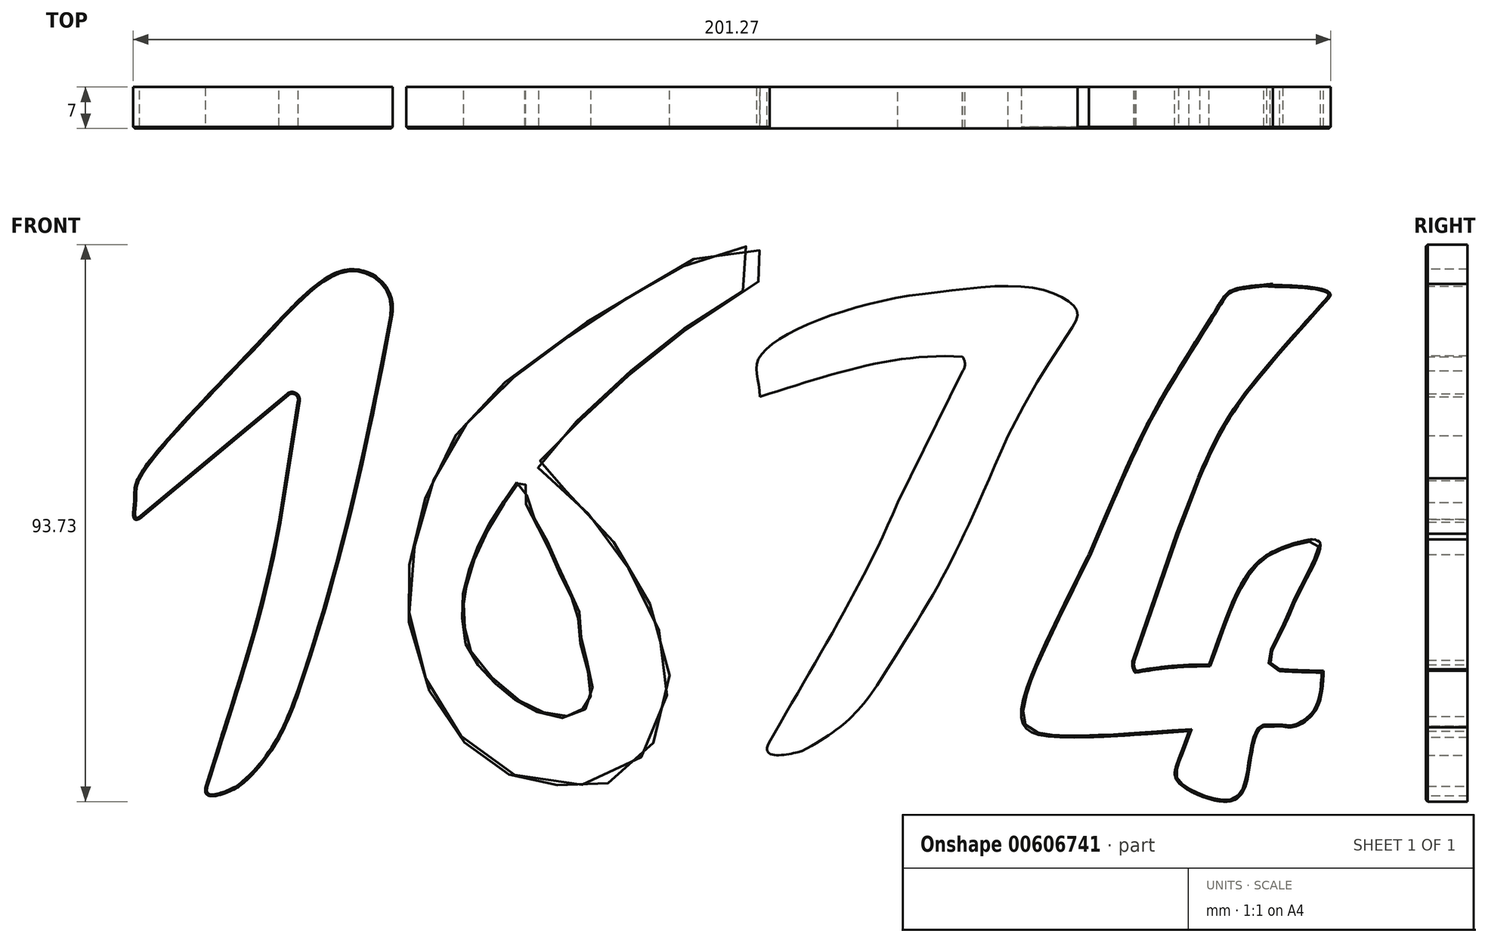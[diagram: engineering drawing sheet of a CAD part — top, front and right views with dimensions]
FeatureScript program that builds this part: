
annotation { "Feature Type Name" : "Feature", "Feature Type Description" : "" }
export const myFeature = defineFeature(function(context is Context, id is Id, definition is map)
    precondition{}
    {
        {
            var Q0;
            Q0=qCreatedBy(makeId("Front.planeOp"),FACE);
            var sketch = newSketch(context, id + "F0", { "sketchPlane" : qUnion([Q0])});
            skLineSegment(sketch, "E0", {"start": v(-92.68, 7.2) * mm, "end": v(-67.67, 28.04) * mm});
            skLineSegment(sketch, "E1", {"start": v(-66.04, 27.11) * mm, "end": v(-69.27, 6.68) * mm});
            skPoint(sketch, "E2.visualSharp", {"position": v(-65.63, 29.74) * mm});
            skArc(sketch, "E2.filletArc", {"start": v(-66.04, 27.11) * mm, "mid": v(-66.53, 28.14) * mm, "end": v(-67.67, 28.04) * mm});
            skFitSpline(sketch, "E3", {"points": [v(-69.27, 6.68) * mm, v(-81.5, -37.64) * mm], "startDerivative": vector(-8.47, -48.32) * mm, "endDerivative": vector(-12.86, -41.9) * mm});
            skFitSpline(sketch, "E4", {"points": [v(-81.5, -37.64) * mm, v(-75.88, -37.8) * mm], "startDerivative": vector(-3.5, -11.42) * mm, "endDerivative": vector(1.2, 0.98) * mm});
            skFitSpline(sketch, "E5", {"points": [v(-65.67, -21.29) * mm, v(-75.88, -37.8) * mm], "startDerivative": vector(-6.02, -17.7) * mm, "endDerivative": vector(-17.03, -13.98) * mm});
            skFitSpline(sketch, "E6", {"points": [v(-65.67, -21.29) * mm, v(-50.24, 41.3) * mm], "startDerivative": vector(20.8, 61.13) * mm, "endDerivative": vector(11.64, 63.63) * mm});
            skFitSpline(sketch, "E7", {"points": [v(-50.24, 41.3) * mm, v(-51.61, 46.83) * mm, v(-58.52, 49.02) * mm, v(-74.86, 34.62) * mm], "startDerivative": vector(4.33, 23.7) * mm, "endDerivative": vector(-40.7, -41.95) * mm});
            skFitSpline(sketch, "E8", {"points": [v(-74.86, 34.62) * mm, v(-93.57, 10.32) * mm, v(-93.56, 7.2) * mm, v(-92.68, 7.2) * mm], "startDerivative": vector(-91.04, -93.86) * mm, "endDerivative": vector(9, 3.05) * mm});
            skFitSpline(sketch, "E9", {"points": [v(-74.86, 34.62) * mm, v(-93.57, 10.32) * mm, v(-93.56, 7.2) * mm, v(-92.68, 7.2) * mm], "startDerivative": vector(-91.04, -93.86) * mm, "endDerivative": vector(9, 3.05) * mm});
            skLineSegment(sketch, "E10", {"start": v(-93.64, 7.35) * mm, "end": v(-93.32, 12.7) * mm});
            skLineSegment(sketch, "E11", {"start": v(-93.32, 12.7) * mm, "end": v(-93, 13.93) * mm});
            skSolve(sketch);
        }
        {
            var Q0;
            Q0=qCreatedBy(makeId("Front.planeOp"),FACE);
            var sketch = newSketch(context, id + "F1", { "sketchPlane" : qUnion([Q0])});
            skFitSpline(sketch, "E12", {"points": [v(-0.98, 38.94) * mm, v(13, 48.92) * mm, v(12.6, 51.28) * mm, v(8.34, 53.38) * mm, v(-20.6, 38.22) * mm, v(-36.6, 24.97) * mm, v(-43.36, 14.2) * mm, v(-47.04, 1.02) * mm, v(-47.76, -6.92) * mm, v(-44.74, -19.9) * mm, v(-39.1, -29.23) * mm, v(-32.6, -34.87) * mm, v(-25.78, -37.1) * mm, v(-19.74, -37.76) * mm, v(-12.33, -36.64) * mm, v(-5.3, -28.44) * mm, v(-4, -15.32) * mm, v(-9.9, -1.54) * mm, v(-17.38, 8.63) * mm, v(-25.06, 15.45) * mm, v(-25.47, 16.76) * mm, v(-20.09, 22.41) * mm, v(-11.63, 30.3) * mm, v(-0.98, 38.94) * mm]});
            skFitSpline(sketch, "E13", {"points": [v(-29.07, 13.15) * mm, v(-31.94, 8.9) * mm, v(-35.91, 1.66) * mm, v(-37.8, -4.45) * mm, v(-38.18, -6.71) * mm, v(-38.01, -11.23) * mm, v(-36.58, -15.81) * mm, v(-29.18, -23.1) * mm, v(-24.22, -25.52) * mm, v(-19.97, -25.86) * mm, v(-18.1, -24.7) * mm, v(-17.05, -23.43) * mm, v(-17.05, -19.46) * mm, v(-18.7, -13.11) * mm, v(-19.09, -8.42) * mm, v(-20.85, -4.5) * mm, v(-22.95, -0.03) * mm, v(-25.27, 5.04) * mm, v(-27.8, 10) * mm, v(-27.8, 13.04) * mm, v(-28.3, 13.64) * mm, v(-29.07, 13.15) * mm]});
            skSolve(sketch);
        }
        {
            var Q0;
            Q0=qCreatedBy(makeId("Front.planeOp"),FACE);
            var sketch = newSketch(context, id + "F2", { "sketchPlane" : qUnion([Q0])});
            skLineSegment(sketch, "E14", {"start": v(45.72, 32.14) * mm, "end": v(34.79, 9.97) * mm});
            skPoint(sketch, "E15.visualSharp", {"position": v(53.05, 42.63) * mm});
            skArc(sketch, "E15.filletArc", {"start": v(45.72, 32.14) * mm, "mid": v(46.07, 33.32) * mm, "end": v(45.66, 34.48) * mm});
            skFitSpline(sketch, "E16", {"points": [v(34.79, 9.97) * mm, v(13.12, -30.48) * mm], "startDerivative": vector(-19.16, -45.24) * mm, "endDerivative": vector(-21.62, -38.5) * mm});
            skFitSpline(sketch, "E17", {"points": [v(13.12, -30.48) * mm, v(18.63, -31.83) * mm], "startDerivative": vector(-5.9, -10.52) * mm, "endDerivative": vector(1.06, 0.55) * mm});
            skFitSpline(sketch, "E18", {"points": [v(31.7, -20.14) * mm, v(18.63, -31.83) * mm], "startDerivative": vector(-10.16, -16) * mm, "endDerivative": vector(-19.7, -10.23) * mm});
            skFitSpline(sketch, "E19", {"points": [v(31.7, -20.14) * mm, v(53.3, 21.22) * mm], "startDerivative": vector(34.21, 53.88) * mm, "endDerivative": vector(26.95, 62.38) * mm});
            skFitSpline(sketch, "E20", {"points": [v(53.3, 21.22) * mm, v(64.68, 42.59) * mm, v(58.21, 45.98) * mm, v(38.9, 45.06) * mm], "startDerivative": vector(64.2, 125.67) * mm, "endDerivative": vector(-57.63, -6.86) * mm});
            skFitSpline(sketch, "E21", {"points": [v(45.66, 34.48) * mm, v(11.57, 27.76) * mm], "startDerivative": vector(-33.68, 2.47) * mm, "endDerivative": vector(-35.46, -11.25) * mm});
            skFitSpline(sketch, "E22", {"points": [v(11.57, 27.76) * mm, v(11.57, 34.48) * mm, v(38.9, 45.06) * mm], "startDerivative": vector(0.24, 25.58) * mm, "endDerivative": vector(50, 5.96) * mm});
            skFitSpline(sketch, "E23", {"points": [v(45.66, 34.48) * mm, v(11.57, 27.76) * mm], "startDerivative": vector(-33.68, 2.47) * mm, "endDerivative": vector(-35.46, -11.25) * mm});
            skSolve(sketch);
        }
        {
            var Q0;
            Q0=qCreatedBy(makeId("Front.planeOp"),FACE);
            var sketch = newSketch(context, id + "F3", { "sketchPlane" : qUnion([Q0])});
            skLineSegment(sketch, "E24", {"start": v(74.6, -16.55) * mm, "end": v(81.93, 4.72) * mm});
            skPoint(sketch, "E25.visualSharp", {"position": v(67.27, -27.04) * mm});
            skArc(sketch, "E25.filletArc", {"start": v(74.6, -16.55) * mm, "mid": v(74.5, -17.48) * mm, "end": v(74.83, -18.36) * mm});
            skFitSpline(sketch, "E26", {"points": [v(83.32, 8.87) * mm, v(107.26, 44.32) * mm], "startDerivative": vector(19.16, 45.24) * mm, "endDerivative": vector(52.3, 57.7) * mm});
            skFitSpline(sketch, "E27", {"points": [v(107.26, 44.32) * mm, v(97.83, 46.76) * mm], "startDerivative": vector(8.1, 8.94) * mm, "endDerivative": vector(16.4, 1.55) * mm});
            skFitSpline(sketch, "E28", {"points": [v(87.26, 40.86) * mm, v(97.83, 46.76) * mm], "startDerivative": vector(10.16, 16) * mm, "endDerivative": vector(25.73, 2.44) * mm});
            skFitSpline(sketch, "E29", {"points": [v(87.26, 40.86) * mm, v(66.87, 1.25) * mm], "startDerivative": vector(-34.21, -53.88) * mm, "endDerivative": vector(-26.95, -62.38) * mm});
            skFitSpline(sketch, "E30", {"points": [v(66.87, 1.25) * mm, v(55.78, -27.18) * mm, v(62.85, -29.56) * mm, v(99.48, -27.7) * mm], "startDerivative": vector(-62.3, -126.61) * mm, "endDerivative": vector(58.88, -0.73) * mm});
            skFitSpline(sketch, "E31", {"points": [v(74.83, -18.36) * mm, v(106.36, -18.33) * mm], "startDerivative": vector(40.38, 7.12) * mm, "endDerivative": vector(38.72, 0) * mm});
            skFitSpline(sketch, "E32", {"points": [v(85.51, 14.03) * mm, v(81.93, 4.72) * mm], "startDerivative": vector(-3.58, -9.32) * mm, "endDerivative": vector(-3.58, -9.32) * mm});
            skFitSpline(sketch, "E33", {"points": [v(66.87, 1.25) * mm, v(55.78, -27.18) * mm, v(62.85, -29.56) * mm, v(99.48, -27.7) * mm], "startDerivative": vector(-62.3, -126.61) * mm, "endDerivative": vector(58.88, -0.73) * mm});
            skFitSpline(sketch, "E34", {"points": [v(87.1, -17.3) * mm, v(95.33, 0) * mm, v(102.56, 3.42) * mm, v(105.76, 3.24) * mm, v(102.25, -5.3) * mm, v(99.17, -12.02) * mm, v(98.95, -18.08) * mm], "startDerivative": vector(34.67, 99.65) * mm, "endDerivative": vector(63.85, -8.51) * mm});
            skFitSpline(sketch, "E35", {"points": [v(96.37, -27.75) * mm, v(94.1, -33.34) * mm, v(91.2, -40.14) * mm, v(82.22, -37.45) * mm, v(83.74, -28.5) * mm], "startDerivative": vector(-17.93, 0) * mm, "endDerivative": vector(24.99, 68.37) * mm});
            skFitSpline(sketch, "E36", {"points": [v(99.48, -27.7) * mm, v(101.43, -27.75) * mm, v(105.02, -25.02) * mm, v(106.36, -18.33) * mm], "startDerivative": vector(7.82, -1.52) * mm, "endDerivative": vector(0.86, 17.28) * mm});
            skSolve(sketch);
        }
        {
            var Q0;
            Q0 = qSketchRegion(id + "F0", true);
            var Q1;
            Q1 = qSketchRegion(id + "F1", true);
            var Q2;
            Q2 = qSketchRegion(id + "F2", true);
            var Q3;
            Q3 = qSketchRegion(id + "F3", true);
            extrude(context, id + "F4", {"entities" : qUnion([Q0, Q1, Q2, Q3]), "depth" : 7 * mm, "offsetDistance" : 25 * mm});
        }
        {
            var Q0;
            Q0=makeQuery(id+"F4.opExtrude","CAP_EDGE",EDGE,{"disambiguationData":[OSD([sQuery(id+"F0.wireOp",EDGE,"E8")])],"isStart":false});
            var Q1;
            Q1=makeQuery(id+"F4.opExtrude","CAP_EDGE",EDGE,{"disambiguationData":[OSD([sQuery(id+"F0.wireOp",EDGE,"E0")])],"isStart":false});
            var Q2;
            Q2=makeQuery(id+"F4.opExtrude","SWEPT_EDGE",EDGE,{"disambiguationData":[OSD([sQuery(id+"F0.wireOp",EDGE,"E10"),sQuery(id+"F0.wireOp",EDGE,"E11")])]});
            var Q3;
            Q3=makeQuery(id+"F4.opExtrude","SWEPT_EDGE",EDGE,{"disambiguationData":[OSD([sQuery(id+"F0.wireOp",EDGE,"E8"),sQuery(id+"F0.wireOp",EDGE,"E11")])]});
            var Q4;
            Q4=makeQuery(id+"F4.opExtrude","CAP_EDGE",EDGE,{"disambiguationData":[OSD([sQuery(id+"F1.wireOp",EDGE,"E12")])],"isStart":false});
            var Q5;
            Q5=makeQuery(id+"F4.opExtrude","CAP_EDGE",EDGE,{"disambiguationData":[OSD([sQuery(id+"F1.wireOp",EDGE,"E13")])],"isStart":false});
            var Q6;
            Q6=makeQuery(id+"F4.opExtrude","CAP_FACE",FACE,{"disambiguationData":[OSD([sQuery(id+"F2.wireOp",EDGE,"E14"),sQuery(id+"F2.wireOp",EDGE,"E15.filletArc"),sQuery(id+"F2.wireOp",EDGE,"E16"),sQuery(id+"F2.wireOp",EDGE,"E17"),sQuery(id+"F2.wireOp",EDGE,"E18"),sQuery(id+"F2.wireOp",EDGE,"E19"),sQuery(id+"F2.wireOp",EDGE,"E20"),sQuery(id+"F2.wireOp",EDGE,"E21"),sQuery(id+"F2.wireOp",EDGE,"E22"),sQuery(id+"F2.wireOp",EDGE,"E23")])],"isStart":false});
            var Q7;
            Q7=makeQuery(id+"F4.opExtrude","CAP_FACE",FACE,{"disambiguationData":[OSD([sQuery(id+"F3.wireOp",EDGE,"E24"),sQuery(id+"F3.wireOp",EDGE,"E25.filletArc"),sQuery(id+"F3.wireOp",EDGE,"E26"),sQuery(id+"F3.wireOp",EDGE,"E27"),sQuery(id+"F3.wireOp",EDGE,"E28"),sQuery(id+"F3.wireOp",EDGE,"E29"),sQuery(id+"F3.wireOp",EDGE,"E30"),sQuery(id+"F3.wireOp",EDGE,"E31"),sQuery(id+"F3.wireOp",EDGE,"E32"),sQuery(id+"F3.wireOp",EDGE,"E31"),sQuery(id+"F3.wireOp",EDGE,"E33"),sQuery(id+"F3.wireOp",EDGE,"E34"),sQuery(id+"F3.wireOp",EDGE,"E35"),sQuery(id+"F3.wireOp",EDGE,"E36")])],"isStart":false});
            chamfer(context, id + "F5", {"entities" : qUnion([Q0, Q1, Q2, Q3, Q4, Q5, Q6, Q7]), "width" : 0.3 * mm, "tangentPropagation" : true});
        }
    });
